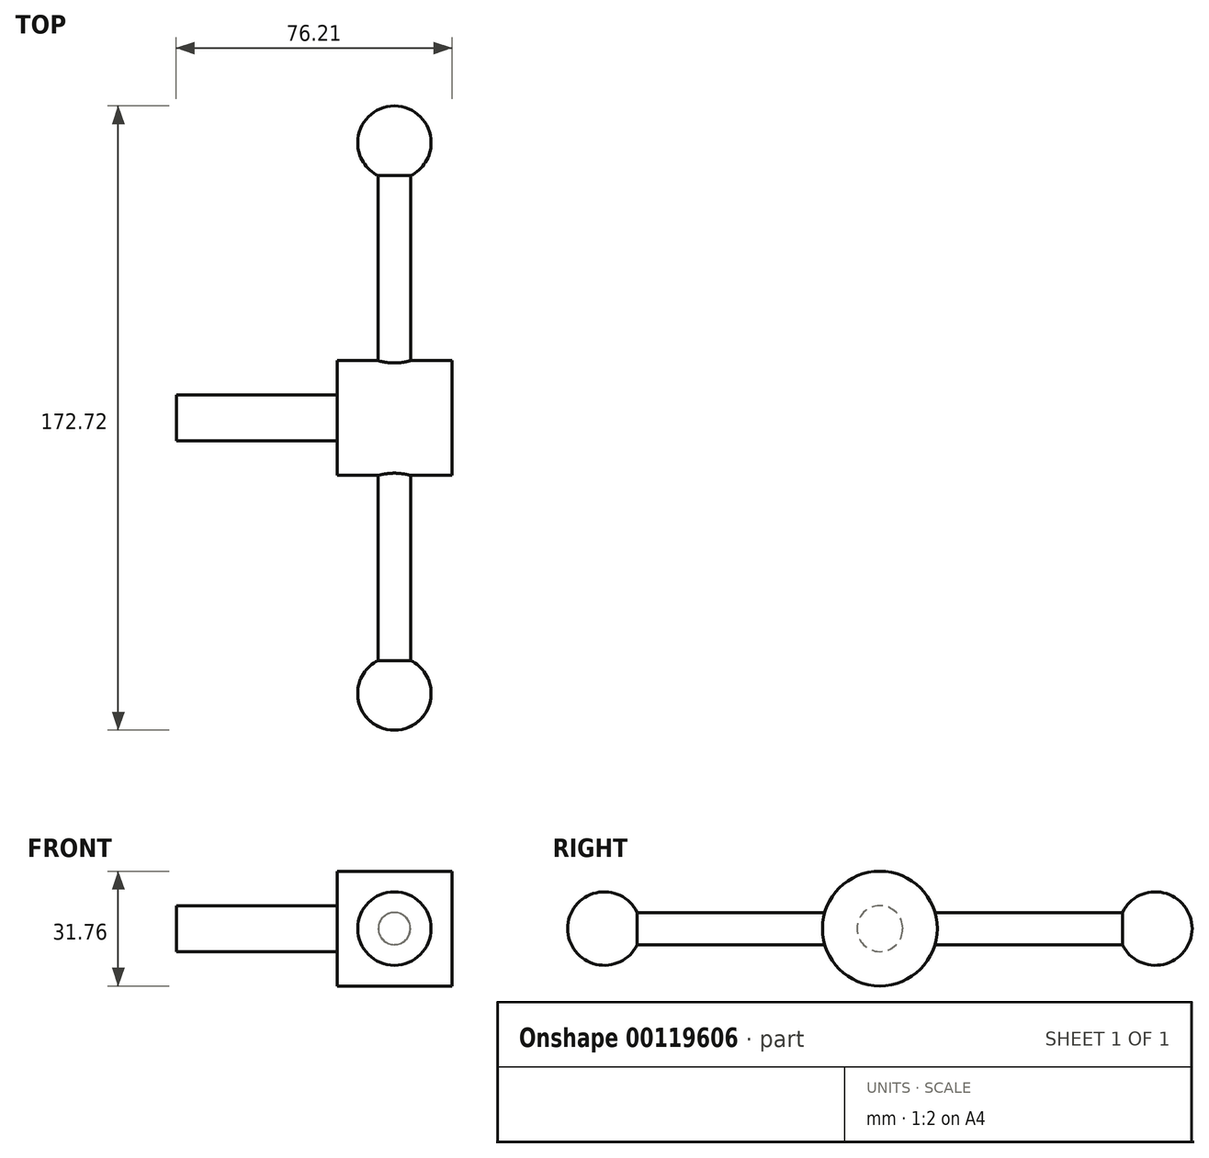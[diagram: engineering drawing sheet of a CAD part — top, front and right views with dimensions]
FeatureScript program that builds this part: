
annotation { "Feature Type Name" : "Feature", "Feature Type Description" : "" }
export const myFeature = defineFeature(function(context is Context, id is Id, definition is map)
    precondition{}
    {
        {
            var Q0;
            Q0=qCreatedBy(makeId("Right.planeOp"),FACE);
            var sketch = newSketch(context, id + "F0", { "sketchPlane" : qUnion([Q0])});
            skCircle(sketch, "E0", {"center": v(0, 0) * mm, "radius": 6.35 * mm});
            skCircle(sketch, "E1", {"center": v(0, 0) * mm, "radius": 15.88 * mm});
            skSolve(sketch);
        }
        {
            var Q0;
            Q0=makeQuery(id+"F0.imprint","IMPRINT",FACE,{"disambiguationData":[TD([[makeQuery(id+"F0.imprint","IMPRINT",EDGE,{"derivedFrom":sQuery(id+"F0.wireOp",EDGE,"E0")}),-1.0]])]});
            extrude(context, id + "F1", {"entities" : qUnion([Q0]), "endBound" : BoundingType.SYMMETRIC, "oppositeDirection" : true, "depth" : 31.75 * mm});
        }
        {
            var Q0;
            Q0=makeQuery(id+"F0.imprint","IMPRINT",FACE,{"disambiguationData":[TD([[makeQuery(id+"F0.imprint","IMPRINT",EDGE,{"derivedFrom":sQuery(id+"F0.wireOp",EDGE,"E0")}),1.0]])]});
            var Q1;
            Q1=makeQuery(id+"F1.opExtrude","CAP_FACE",FACE,{"disambiguationData":[OSD([sQuery(id+"F0.wireOp",EDGE,"E0"),sQuery(id+"F0.wireOp",EDGE,"E1")])],"isStart":true});
            extrude(context, id + "F2", {"entities" : qUnion([Q0]), "operationType" : NewBodyOperationType.ADD, "oppositeDirection" : true, "depth" : 60.32 * mm, "hasSecondDirection" : true, "secondDirectionBound" : SecondDirectionBoundingType.UP_TO_SURFACE, "secondDirectionOppositeDirection" : false, "secondDirectionBoundEntityFace" : qUnion([Q1]), "secondDirectionDepth" : 25.4 * mm});
        }
        {
            var Q0;
            Q0=qCreatedBy(makeId("Front.planeOp"),FACE);
            var sketch = newSketch(context, id + "F3", { "sketchPlane" : qUnion([Q0])});
            skCircle(sketch, "E2", {"center": v(0, 0) * mm, "radius": 4.45 * mm});
            skSolve(sketch);
        }
        {
            var Q0;
            Q0 = qSketchRegion(id + "F3", true);
            extrude(context, id + "F4", {"entities" : qUnion([Q0]), "operationType" : NewBodyOperationType.ADD, "endBound" : BoundingType.SYMMETRIC, "depth" : 152.4 * mm});
        }
        {
            var Q0;
            Q0=qCreatedBy(makeId("Top.planeOp"),FACE);
            var sketch = newSketch(context, id + "F5", { "sketchPlane" : qUnion([Q0])});
            skLineSegment(sketch, "E3", {"start": v(0, 103.1) * mm, "end": v(0, -100.1) * mm, "construction": true});
            skArc(sketch, "E4", {"start": v(10.16, 76.2) * mm, "mid": v(0, 86.36) * mm, "end": v(-10.16, 76.2) * mm});
            skLineSegment(sketch, "E5", {"start": v(-10.16, 76.2) * mm, "end": v(10.16, 76.2) * mm});
            skLineSegment(sketch, "E6", {"start": v(-76.72, 0) * mm, "end": v(73.66, 0) * mm, "construction": true});
            skLineSegment(sketch, "E7.MirrorCS", {"start": v(-10.16, -76.2) * mm, "end": v(10.16, -76.2) * mm});
            skArc(sketch, "E8.MirrorCS", {"start": v(10.16, -76.2) * mm, "mid": v(0, -86.36) * mm, "end": v(-10.16, -76.2) * mm});
            skSolve(sketch);
        }
        {
            var Q0;
            Q0=makeQuery(id+"F5.imprint","IMPRINT",FACE,{"disambiguationData":[TD([[makeQuery(id+"F5.imprint","IMPRINT",EDGE,{"derivedFrom":sQuery(id+"F5.wireOp",EDGE,"E7.MirrorCS")}),-1.0]])]});
            var Q1;
            Q1=sQuery(id+"F5.wireOp",EDGE,"E7.MirrorCS");
            revolve(context, id + "F6", {"operationType" : NewBodyOperationType.ADD, "entities" : qUnion([Q0]), "axis" : qUnion([Q1]), "revolveType" : RevolveType.FULL});
        }
        {
            var Q0;
            Q0=makeQuery(id+"F5.imprint","IMPRINT",FACE,{"disambiguationData":[TD([[makeQuery(id+"F5.imprint","IMPRINT",EDGE,{"derivedFrom":sQuery(id+"F5.wireOp",EDGE,"E4")}),1.0]])]});
            var Q1;
            Q1=sQuery(id+"F5.wireOp",EDGE,"E5");
            revolve(context, id + "F7", {"operationType" : NewBodyOperationType.ADD, "entities" : qUnion([Q0]), "axis" : qUnion([Q1]), "revolveType" : RevolveType.FULL});
        }
    });
